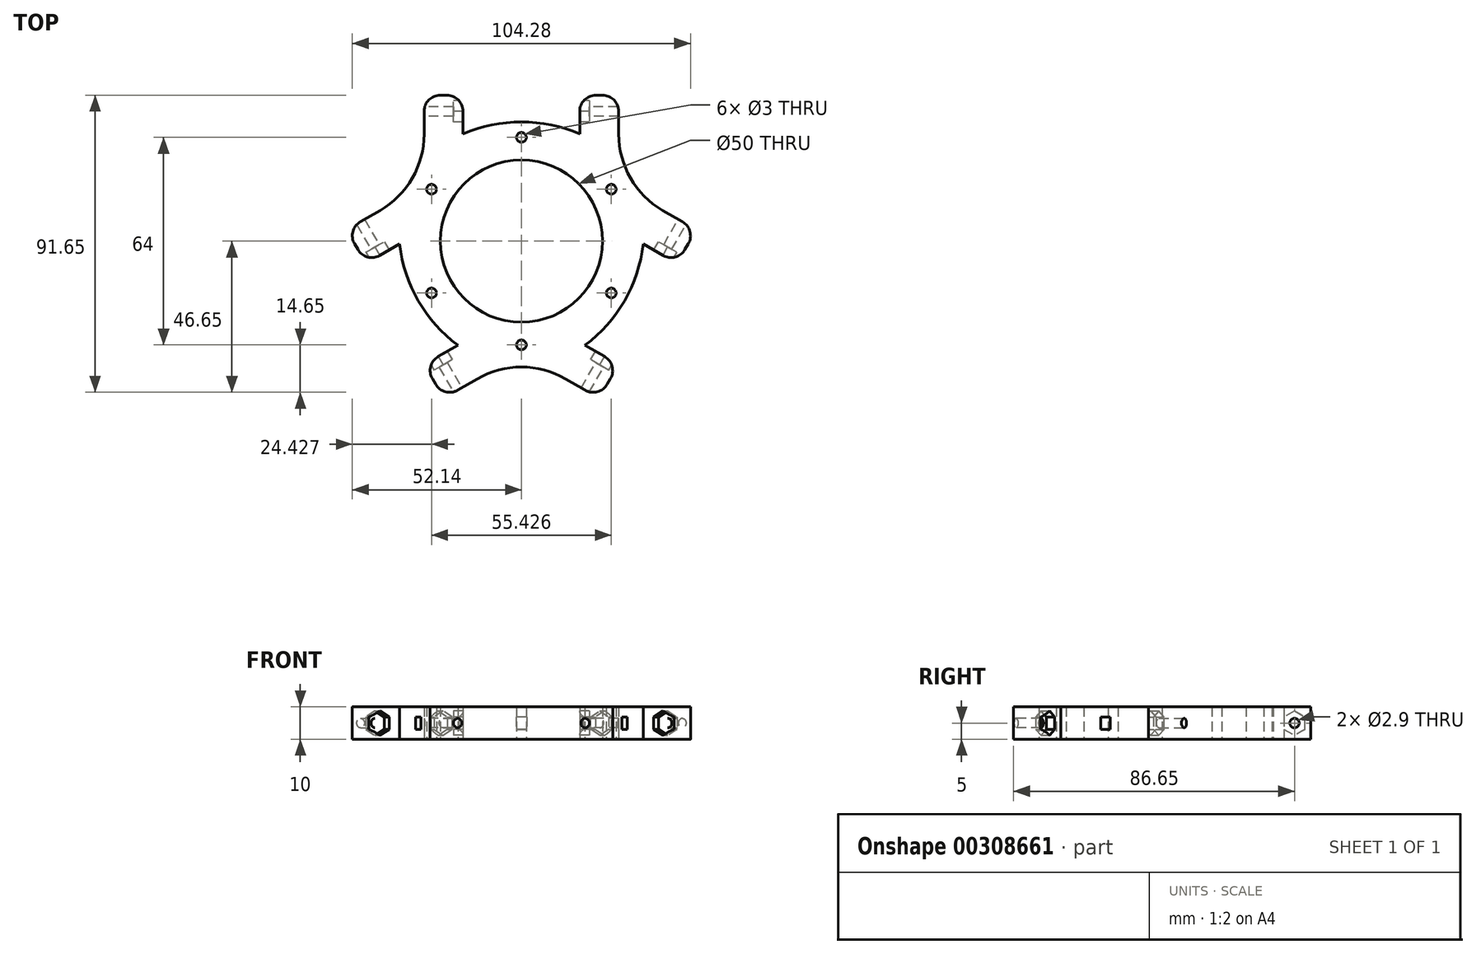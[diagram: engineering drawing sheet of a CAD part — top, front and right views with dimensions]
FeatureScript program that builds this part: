
annotation { "Feature Type Name" : "Feature", "Feature Type Description" : "" }
export const myFeature = defineFeature(function(context is Context, id is Id, definition is map)
    precondition{}
    {
        {
            var Q0;
            Q0=qCreatedBy(makeId("Top.planeOp"),FACE);
            var sketch = newSketch(context, id + "F0", { "sketchPlane" : qUnion([Q0])});
            skLineSegment(sketch, "E0", {"start": v(0, 0) * mm, "end": v(0, 45) * mm});
            skLineSegment(sketch, "E1", {"start": v(0, 0) * mm, "end": v(-38.97, -22.5) * mm});
            skLineSegment(sketch, "E2", {"start": v(0, 0) * mm, "end": v(31.83, -18.38) * mm});
            skLineSegment(sketch, "E3", {"start": v(18, 45) * mm, "end": v(30, 45) * mm});
            skLineSegment(sketch, "E4.MirrorCS", {"start": v(-18, 45) * mm, "end": v(-30, 45) * mm});
            skLineSegment(sketch, "E5", {"start": v(-47.97, -6.91) * mm, "end": v(-53.97, 3.48) * mm});
            skLineSegment(sketch, "E6.MirrorCS", {"start": v(-29.97, -38.09) * mm, "end": v(-23.97, -48.48) * mm});
            skLineSegment(sketch, "E7", {"start": v(47.97, -6.91) * mm, "end": v(53.97, 3.48) * mm});
            skLineSegment(sketch, "E8.MirrorCS", {"start": v(29.97, -38.09) * mm, "end": v(23.97, -48.48) * mm});
            skLineSegment(sketch, "E9", {"start": v(-30, 45) * mm, "end": v(-30, 33) * mm});
            skLineSegment(sketch, "E10", {"start": v(-53.97, 3.48) * mm, "end": v(-43.58, 9.48) * mm});
            skLineSegment(sketch, "E11", {"start": v(23.97, -48.48) * mm, "end": v(13.58, -42.48) * mm});
            skLineSegment(sketch, "E12.MirrorCS", {"start": v(30, 45) * mm, "end": v(30, 33) * mm});
            skLineSegment(sketch, "E13.MirrorCS", {"start": v(-23.97, -48.48) * mm, "end": v(-13.58, -42.48) * mm});
            skLineSegment(sketch, "E14.MirrorCS", {"start": v(53.97, 3.48) * mm, "end": v(43.58, 9.48) * mm});
            skCircle(sketch, "E15", {"center": v(0, 0) * mm, "radius": 25 * mm});
            skLineSegment(sketch, "E16", {"start": v(0, 0) * mm, "end": v(33.64, 19.42) * mm});
            skLineSegment(sketch, "E17", {"start": v(0, 0) * mm, "end": v(-33.64, 19.42) * mm});
            skLineSegment(sketch, "E18", {"start": v(0, 0) * mm, "end": v(0, -42.48) * mm});
            skCircle(sketch, "E19", {"center": v(27.71, 16) * mm, "radius": 1.5 * mm});
            skCircle(sketch, "E20", {"center": v(0, -32) * mm, "radius": 1.5 * mm});
            skCircle(sketch, "E21", {"center": v(-27.71, 16) * mm, "radius": 1.5 * mm});
            skLineSegment(sketch, "E22", {"start": v(18, 45) * mm, "end": v(18, 33) * mm});
            skLineSegment(sketch, "E23.MirrorCS", {"start": v(-18, 45) * mm, "end": v(-18, 33) * mm});
            skArc(sketch, "E24", {"start": v(18, 33) * mm, "mid": v(0, 36.76) * mm, "end": v(-18, 33) * mm});
            skLineSegment(sketch, "E25", {"start": v(47.97, -6.91) * mm, "end": v(37.58, -0.91) * mm});
            skLineSegment(sketch, "E26.MirrorCS", {"start": v(29.97, -38.09) * mm, "end": v(19.58, -32.09) * mm});
            skArc(sketch, "E27", {"start": v(19.58, -32.09) * mm, "mid": v(31.83, -18.38) * mm, "end": v(37.58, -0.91) * mm});
            skLineSegment(sketch, "E28", {"start": v(-29.97, -38.09) * mm, "end": v(-19.58, -32.09) * mm});
            skLineSegment(sketch, "E29.MirrorCS", {"start": v(-47.97, -6.91) * mm, "end": v(-37.58, -0.91) * mm});
            skArc(sketch, "E30", {"start": v(-37.58, -0.91) * mm, "mid": v(-31.83, -18.38) * mm, "end": v(-19.58, -32.09) * mm});
            skArc(sketch, "E31", {"start": v(-43.58, 9.48) * mm, "mid": v(-33.64, 19.42) * mm, "end": v(-30, 33) * mm});
            skArc(sketch, "E32", {"start": v(30, 33) * mm, "mid": v(33.64, 19.42) * mm, "end": v(43.58, 9.48) * mm});
            skArc(sketch, "E33", {"start": v(13.58, -42.48) * mm, "mid": v(0, -38.84) * mm, "end": v(-13.58, -42.48) * mm});
            skPoint(sketch, "E34.orphan", {"position": v(-36.79, 21.24) * mm});
            skPoint(sketch, "E35.orphan", {"position": v(0, 45) * mm});
            skPoint(sketch, "E36.orphan", {"position": v(-38.97, -22.5) * mm});
            skCircle(sketch, "E37", {"center": v(-27.71, -16) * mm, "radius": 1.5 * mm});
            skCircle(sketch, "E38", {"center": v(27.71, -16) * mm, "radius": 1.5 * mm});
            skCircle(sketch, "E39", {"center": v(0, 32) * mm, "radius": 1.5 * mm});
            skSolve(sketch);
        }
        {
            var Q0;
            {var subQ4=sQuery(id+"F0.wireOp",EDGE,"E4.MirrorCS");Q0=makeQuery(id+"F0.imprint","IMPRINT",FACE,{"disambiguationData":[TD([[makeQuery(id+"F0.imprint","IMPRINT",EDGE,{"derivedFrom":subQ4}),1.0]])]});}
            var Q1;
            {var subQ0=sQuery(id+"F0.wireOp",EDGE,"E6.MirrorCS");Q1=makeQuery(id+"F0.imprint","IMPRINT",FACE,{"disambiguationData":[TD([[makeQuery(id+"F0.imprint","IMPRINT",EDGE,{"derivedFrom":subQ0}),1.0]])]});}
            var Q2;
            {var subQ4=sQuery(id+"F0.wireOp",EDGE,"E3");Q2=makeQuery(id+"F0.imprint","IMPRINT",FACE,{"disambiguationData":[TD([[makeQuery(id+"F0.imprint","IMPRINT",EDGE,{"derivedFrom":subQ4}),-1.0]])]});}
            var Q3;
            {var subQ1=sQuery(id+"F0.wireOp",EDGE,"E7");Q3=makeQuery(id+"F0.imprint","IMPRINT",FACE,{"disambiguationData":[TD([[makeQuery(id+"F0.imprint","IMPRINT",EDGE,{"derivedFrom":subQ1}),1.0]])]});}
            var Q4;
            Q4=makeQuery(id+"F0.imprint","IMPRINT",FACE,{"disambiguationData":[TD([[makeQuery(id+"F0.imprint","IMPRINT",EDGE,{"derivedFrom":sQuery(id+"F0.wireOp",EDGE,"93i2Dirp-5Tey-j3A0-DUrq-3imIRp9fQiXa")}),1.0]])]});
            var Q5;
            {var subQ0=sQuery(id+"F0.wireOp",EDGE,"E1");var subQ1=sQuery(id+"F0.wireOp",EDGE,"7GjnHj9b-fa3a-kwGP-agom-r8laERjyn4mw");var subQ2=makeQuery(id+"F0.imprint","INTERSECT",VERTEX,{"derivedFrom":[subQ1,subQ0]});Q5=makeQuery(id+"F0.imprint","IMPRINT",FACE,{"disambiguationData":[TD([[makeQuery(id+"F0.imprint","IMPRINT",EDGE,{"disambiguationData":[TD([[subQ2,1.0]])],"derivedFrom":subQ1}),1.0]])]});}
            var Q6;
            {var subQ0=sQuery(id+"F0.wireOp",EDGE,"E0");var subQ1=sQuery(id+"F0.wireOp",EDGE,"7GjnHj9b-fa3a-kwGP-agom-r8laERjyn4mw");var subQ2=makeQuery(id+"F0.imprint","INTERSECT",VERTEX,{"derivedFrom":[subQ1,subQ0]});Q6=makeQuery(id+"F0.imprint","IMPRINT",FACE,{"disambiguationData":[TD([[makeQuery(id+"F0.imprint","IMPRINT",EDGE,{"disambiguationData":[TD([[subQ2,1.0]])],"derivedFrom":subQ1}),1.0]])]});}
            var Q7;
            {var subQ0=sQuery(id+"F0.wireOp",EDGE,"E1");var subQ1=sQuery(id+"F0.wireOp",EDGE,"7GjnHj9b-fa3a-kwGP-agom-r8laERjyn4mw");var subQ2=makeQuery(id+"F0.imprint","INTERSECT",VERTEX,{"derivedFrom":[subQ1,subQ0]});Q7=makeQuery(id+"F0.imprint","IMPRINT",FACE,{"disambiguationData":[TD([[makeQuery(id+"F0.imprint","IMPRINT",EDGE,{"disambiguationData":[TD([[subQ2,-1.0]])],"derivedFrom":subQ1}),1.0]])]});}
            var Q8;
            {var subQ4=sQuery(id+"F0.wireOp",EDGE,"E5");Q8=makeQuery(id+"F0.imprint","IMPRINT",FACE,{"disambiguationData":[TD([[makeQuery(id+"F0.imprint","IMPRINT",EDGE,{"derivedFrom":subQ4}),-1.0]])]});}
            var Q9;
            {var subQ4=sQuery(id+"F0.wireOp",EDGE,"E8.MirrorCS");Q9=makeQuery(id+"F0.imprint","IMPRINT",FACE,{"disambiguationData":[TD([[makeQuery(id+"F0.imprint","IMPRINT",EDGE,{"derivedFrom":subQ4}),-1.0]])]});}
            extrude(context, id + "F1", {"entities" : qUnion([Q0, Q1, Q2, Q3, Q4, Q5, Q6, Q7, Q8, Q9]), "depth" : 10 * mm});
        }
        {
            var Q0;
            Q0=qCreatedBy(makeId("Right.planeOp"),FACE);
            var sketch = newSketch(context, id + "F2", { "sketchPlane" : qUnion([Q0])});
            skCircle(sketch, "E40", {"center": v(40, 5) * mm, "radius": 1.45 * mm});
            skCircle(sketch, "E41.cCircle", {"center": v(40, 5) * mm, "radius": 3.28 * mm, "construction": true});
            skLineSegment(sketch, "E41.0", {"start": v(43.28, 6.9) * mm, "end": v(43.28, 3.1) * mm});
            skLineSegment(sketch, "E41.1", {"start": v(43.27, 3.1) * mm, "end": v(40, 1.22) * mm});
            skLineSegment(sketch, "E41.2", {"start": v(40, 1.22) * mm, "end": v(36.72, 3.1) * mm});
            skLineSegment(sketch, "E41.3", {"start": v(36.72, 3.1) * mm, "end": v(36.72, 6.9) * mm});
            skLineSegment(sketch, "E41.4", {"start": v(36.72, 6.9) * mm, "end": v(40, 8.78) * mm});
            skLineSegment(sketch, "E41.5", {"start": v(40, 8.78) * mm, "end": v(43.28, 6.9) * mm});
            skPoint(sketch, "E41.0.midPoint", {"position": v(43.28, 5) * mm});
            skSolve(sketch);
        }
        {
            var Q0;
            Q0=makeQuery(id+"F2.imprint","IMPRINT",FACE,{"disambiguationData":[TD([[makeQuery(id+"F2.imprint","IMPRINT",EDGE,{"derivedFrom":sQuery(id+"F2.wireOp",EDGE,"E40")}),1.0]])]});
            extrude(context, id + "F3", {"entities" : qUnion([Q0]), "depth" : 30 * mm, "hasSecondDirection" : true, "secondDirectionOppositeDirection" : true, "secondDirectionDepth" : 30 * mm});
        }
        {
            var Q0;
            Q0=makeQuery(id+"F3.opExtrude","SWEPT_BODY",BODY,{"disambiguationData":[OSD([sQuery(id+"F2.wireOp",EDGE,"E40")])]});
            var Q1;
            Q1=makeQuery(id+"F1.opExtrude","CAP_EDGE",EDGE,{"disambiguationData":[OSD([sQuery(id+"F0.wireOp",EDGE,"E15")])],"isStart":false});
            transform(context, id + "F4", {"entities" : qUnion([Q0]), "transformType" : TransformType.ROTATION, "transformAxis" : qUnion([Q1]), "angle" : 120 * degree, "makeCopy" : true});
        }
        {
            var Q0;
            Q0=makeQuery(id+"F4.opPattern","COPY",BODY,{"derivedFrom":makeQuery(id+"F3.opExtrude","SWEPT_BODY",BODY,{"disambiguationData":[OSD([sQuery(id+"F2.wireOp",EDGE,"E40")])]}),"instanceName":"1"});
            var Q1;
            Q1=makeQuery(id+"F1.opExtrude","CAP_EDGE",EDGE,{"disambiguationData":[OSD([sQuery(id+"F0.wireOp",EDGE,"E15")])],"isStart":false});
            transform(context, id + "F5", {"entities" : qUnion([Q0]), "transformType" : TransformType.ROTATION, "transformAxis" : qUnion([Q1]), "angle" : 120 * degree, "makeCopy" : true});
        }
        {
            var Q0;
            Q0=makeQuery(id+"F5.opPattern","COPY",BODY,{"derivedFrom":makeQuery(id+"F4.opPattern","COPY",BODY,{"derivedFrom":makeQuery(id+"F3.opExtrude","SWEPT_BODY",BODY,{"disambiguationData":[OSD([sQuery(id+"F2.wireOp",EDGE,"E40")])]}),"instanceName":"1"}),"instanceName":"1"});
            var Q1;
            Q1=makeQuery(id+"F3.opExtrude","SWEPT_BODY",BODY,{"disambiguationData":[OSD([sQuery(id+"F2.wireOp",EDGE,"E40")])]});
            var Q2;
            Q2=makeQuery(id+"F4.opPattern","COPY",BODY,{"derivedFrom":makeQuery(id+"F3.opExtrude","SWEPT_BODY",BODY,{"disambiguationData":[OSD([sQuery(id+"F2.wireOp",EDGE,"E40")])]}),"instanceName":"1"});
            var Q3;
            Q3=makeQuery(id+"F1.opExtrude","SWEPT_BODY",BODY,{"disambiguationData":[OSD([sQuery(id+"F0.wireOp",EDGE,"E3"),sQuery(id+"F0.wireOp",EDGE,"E4.MirrorCS"),sQuery(id+"F0.wireOp",EDGE,"E5"),sQuery(id+"F0.wireOp",EDGE,"E6.MirrorCS"),sQuery(id+"F0.wireOp",EDGE,"E7"),sQuery(id+"F0.wireOp",EDGE,"E8.MirrorCS"),sQuery(id+"F0.wireOp",EDGE,"E9"),sQuery(id+"F0.wireOp",EDGE,"E10"),sQuery(id+"F0.wireOp",EDGE,"E11"),sQuery(id+"F0.wireOp",EDGE,"E12.MirrorCS"),sQuery(id+"F0.wireOp",EDGE,"E13.MirrorCS"),sQuery(id+"F0.wireOp",EDGE,"E14.MirrorCS"),sQuery(id+"F0.wireOp",EDGE,"2t7xqRWb-bub8-eMNz-FE5e-p0023Oxu7Jbf"),sQuery(id+"F0.wireOp",EDGE,"vDAQe0BX-fdkM-CdWa-sWsN-lsCfwyhql2Up"),sQuery(id+"F0.wireOp",EDGE,"93i2Dirp-5Tey-j3A0-DUrq-3imIRp9fQiXa"),sQuery(id+"F0.wireOp",EDGE,"QqLDhM0M-4ZeX-t9WL-vnuS-0Zj9XB7gyNKe")])]});
            booleanBodies(context, id + "F6", {"operationType" : BooleanOperationType.SUBTRACTION, "tools" : qUnion([Q0, Q1, Q2]), "targets" : qUnion([Q3])});
        }
        {
            var Q0;
            Q0=makeQuery(id+"F1.opExtrude","SWEPT_EDGE",EDGE,{"disambiguationData":[OSD([sQuery(id+"F0.wireOp",EDGE,"E6.MirrorCS"),sQuery(id+"F0.wireOp",EDGE,"E13.MirrorCS")])]});
            var Q1;
            Q1=makeQuery(id+"F1.opExtrude","SWEPT_EDGE",EDGE,{"disambiguationData":[OSD([sQuery(id+"F0.wireOp",EDGE,"E8.MirrorCS"),sQuery(id+"F0.wireOp",EDGE,"E11")])]});
            var Q2;
            Q2=makeQuery(id+"F1.opExtrude","SWEPT_EDGE",EDGE,{"disambiguationData":[OSD([sQuery(id+"F0.wireOp",EDGE,"E7"),sQuery(id+"F0.wireOp",EDGE,"E14.MirrorCS")])]});
            var Q3;
            Q3=makeQuery(id+"F1.opExtrude","SWEPT_EDGE",EDGE,{"disambiguationData":[OSD([sQuery(id+"F0.wireOp",EDGE,"E3"),sQuery(id+"F0.wireOp",EDGE,"E12.MirrorCS")])]});
            var Q4;
            Q4=makeQuery(id+"F1.opExtrude","SWEPT_EDGE",EDGE,{"disambiguationData":[OSD([sQuery(id+"F0.wireOp",EDGE,"E4.MirrorCS"),sQuery(id+"F0.wireOp",EDGE,"E9")])]});
            var Q5;
            Q5=makeQuery(id+"F1.opExtrude","SWEPT_EDGE",EDGE,{"disambiguationData":[OSD([sQuery(id+"F0.wireOp",EDGE,"E5"),sQuery(id+"F0.wireOp",EDGE,"E10")])]});
            var Q6;
            Q6=makeQuery(id+"F1.opExtrude","SWEPT_EDGE",EDGE,{"disambiguationData":[OSD([sQuery(id+"F0.wireOp",EDGE,"E8.MirrorCS"),sQuery(id+"F0.wireOp",EDGE,"E26.MirrorCS")])]});
            var Q7;
            Q7=makeQuery(id+"F1.opExtrude","SWEPT_EDGE",EDGE,{"disambiguationData":[OSD([sQuery(id+"F0.wireOp",EDGE,"E7"),sQuery(id+"F0.wireOp",EDGE,"E25")])]});
            var Q8;
            Q8=makeQuery(id+"F1.opExtrude","SWEPT_EDGE",EDGE,{"disambiguationData":[OSD([sQuery(id+"F0.wireOp",EDGE,"E3"),sQuery(id+"F0.wireOp",EDGE,"E22")])]});
            var Q9;
            Q9=makeQuery(id+"F1.opExtrude","SWEPT_EDGE",EDGE,{"disambiguationData":[OSD([sQuery(id+"F0.wireOp",EDGE,"E4.MirrorCS"),sQuery(id+"F0.wireOp",EDGE,"E23.MirrorCS")])]});
            var Q10;
            Q10=makeQuery(id+"F1.opExtrude","SWEPT_EDGE",EDGE,{"disambiguationData":[OSD([sQuery(id+"F0.wireOp",EDGE,"E5"),sQuery(id+"F0.wireOp",EDGE,"E29.MirrorCS")])]});
            var Q11;
            Q11=makeQuery(id+"F1.opExtrude","SWEPT_EDGE",EDGE,{"disambiguationData":[OSD([sQuery(id+"F0.wireOp",EDGE,"E6.MirrorCS"),sQuery(id+"F0.wireOp",EDGE,"E28")])]});
            fillet(context, id + "F7", {"entities" : qUnion([Q0, Q1, Q2, Q3, Q4, Q5, Q6, Q7, Q8, Q9, Q10, Q11]), "radius" : 5 * mm, "tangentPropagation" : true, "allowEdgeOverflow" : false});
        }
        {
            var Q0;
            Q0=makeQuery(id+"F2.imprint","IMPRINT",FACE,{"disambiguationData":[TD([[makeQuery(id+"F2.imprint","IMPRINT",EDGE,{"derivedFrom":sQuery(id+"F2.wireOp",EDGE,"E40")}),-1.0]])]});
            extrude(context, id + "F8", {"entities" : qUnion([Q0]), "depth" : 21 * mm, "hasSecondDirection" : true, "secondDirectionOppositeDirection" : true, "secondDirectionDepth" : 21 * mm});
        }
        {
            var Q0;
            Q0=makeQuery(id+"F8.opExtrude","SWEPT_BODY",BODY,{"disambiguationData":[OSD([sQuery(id+"F2.wireOp",EDGE,"E40"),sQuery(id+"F2.wireOp",EDGE,"E41.0"),sQuery(id+"F2.wireOp",EDGE,"E41.1"),sQuery(id+"F2.wireOp",EDGE,"E41.2"),sQuery(id+"F2.wireOp",EDGE,"E41.3"),sQuery(id+"F2.wireOp",EDGE,"E41.4"),sQuery(id+"F2.wireOp",EDGE,"E41.5")])]});
            var Q1;
            Q1=makeQuery(id+"F1.opExtrude","CAP_EDGE",EDGE,{"disambiguationData":[OSD([sQuery(id+"F0.wireOp",EDGE,"E15")])],"isStart":false});
            transform(context, id + "F9", {"entities" : qUnion([Q0]), "transformType" : TransformType.ROTATION, "transformAxis" : qUnion([Q1]), "angle" : 120 * degree, "makeCopy" : true});
        }
        {
            var Q0;
            Q0=makeQuery(id+"F9.opPattern","COPY",BODY,{"derivedFrom":makeQuery(id+"F8.opExtrude","SWEPT_BODY",BODY,{"disambiguationData":[OSD([sQuery(id+"F2.wireOp",EDGE,"E40"),sQuery(id+"F2.wireOp",EDGE,"E41.0"),sQuery(id+"F2.wireOp",EDGE,"E41.1"),sQuery(id+"F2.wireOp",EDGE,"E41.2"),sQuery(id+"F2.wireOp",EDGE,"E41.3"),sQuery(id+"F2.wireOp",EDGE,"E41.4"),sQuery(id+"F2.wireOp",EDGE,"E41.5")])]}),"instanceName":"1"});
            var Q1;
            Q1=makeQuery(id+"F1.opExtrude","CAP_EDGE",EDGE,{"disambiguationData":[OSD([sQuery(id+"F0.wireOp",EDGE,"E15")])],"isStart":false});
            transform(context, id + "F10", {"entities" : qUnion([Q0]), "transformType" : TransformType.ROTATION, "transformAxis" : qUnion([Q1]), "angle" : 120 * degree, "makeCopy" : true});
        }
        {
            var Q0;
            Q0=makeQuery(id+"F8.opExtrude","SWEPT_BODY",BODY,{"disambiguationData":[OSD([sQuery(id+"F2.wireOp",EDGE,"E40"),sQuery(id+"F2.wireOp",EDGE,"E41.0"),sQuery(id+"F2.wireOp",EDGE,"E41.1"),sQuery(id+"F2.wireOp",EDGE,"E41.2"),sQuery(id+"F2.wireOp",EDGE,"E41.3"),sQuery(id+"F2.wireOp",EDGE,"E41.4"),sQuery(id+"F2.wireOp",EDGE,"E41.5")])]});
            var Q1;
            Q1=makeQuery(id+"F10.opPattern","COPY",BODY,{"derivedFrom":makeQuery(id+"F9.opPattern","COPY",BODY,{"derivedFrom":makeQuery(id+"F8.opExtrude","SWEPT_BODY",BODY,{"disambiguationData":[OSD([sQuery(id+"F2.wireOp",EDGE,"E40"),sQuery(id+"F2.wireOp",EDGE,"E41.0"),sQuery(id+"F2.wireOp",EDGE,"E41.1"),sQuery(id+"F2.wireOp",EDGE,"E41.2"),sQuery(id+"F2.wireOp",EDGE,"E41.3"),sQuery(id+"F2.wireOp",EDGE,"E41.4"),sQuery(id+"F2.wireOp",EDGE,"E41.5")])]}),"instanceName":"1"}),"instanceName":"1"});
            var Q2;
            Q2=makeQuery(id+"F9.opPattern","COPY",BODY,{"derivedFrom":makeQuery(id+"F8.opExtrude","SWEPT_BODY",BODY,{"disambiguationData":[OSD([sQuery(id+"F2.wireOp",EDGE,"E40"),sQuery(id+"F2.wireOp",EDGE,"E41.0"),sQuery(id+"F2.wireOp",EDGE,"E41.1"),sQuery(id+"F2.wireOp",EDGE,"E41.2"),sQuery(id+"F2.wireOp",EDGE,"E41.3"),sQuery(id+"F2.wireOp",EDGE,"E41.4"),sQuery(id+"F2.wireOp",EDGE,"E41.5")])]}),"instanceName":"1"});
            var Q3;
            Q3=makeQuery(id+"F1.opExtrude","SWEPT_BODY",BODY,{"disambiguationData":[OSD([sQuery(id+"F0.wireOp",EDGE,"E3"),sQuery(id+"F0.wireOp",EDGE,"E4.MirrorCS"),sQuery(id+"F0.wireOp",EDGE,"E5"),sQuery(id+"F0.wireOp",EDGE,"E6.MirrorCS"),sQuery(id+"F0.wireOp",EDGE,"E7"),sQuery(id+"F0.wireOp",EDGE,"E8.MirrorCS"),sQuery(id+"F0.wireOp",EDGE,"E9"),sQuery(id+"F0.wireOp",EDGE,"E10"),sQuery(id+"F0.wireOp",EDGE,"E11"),sQuery(id+"F0.wireOp",EDGE,"E12.MirrorCS"),sQuery(id+"F0.wireOp",EDGE,"E13.MirrorCS"),sQuery(id+"F0.wireOp",EDGE,"E14.MirrorCS"),sQuery(id+"F0.wireOp",EDGE,"E15"),sQuery(id+"F0.wireOp",EDGE,"E19"),sQuery(id+"F0.wireOp",EDGE,"E20"),sQuery(id+"F0.wireOp",EDGE,"E21"),sQuery(id+"F0.wireOp",EDGE,"E22"),sQuery(id+"F0.wireOp",EDGE,"E23.MirrorCS"),sQuery(id+"F0.wireOp",EDGE,"E24"),sQuery(id+"F0.wireOp",EDGE,"E25"),sQuery(id+"F0.wireOp",EDGE,"E26.MirrorCS"),sQuery(id+"F0.wireOp",EDGE,"E27"),sQuery(id+"F0.wireOp",EDGE,"E28"),sQuery(id+"F0.wireOp",EDGE,"E29.MirrorCS"),sQuery(id+"F0.wireOp",EDGE,"E30"),sQuery(id+"F0.wireOp",EDGE,"E31"),sQuery(id+"F0.wireOp",EDGE,"E32"),sQuery(id+"F0.wireOp",EDGE,"E33"),sQuery(id+"F0.wireOp",EDGE,"E37"),sQuery(id+"F0.wireOp",EDGE,"E38"),sQuery(id+"F0.wireOp",EDGE,"E39")])]});
            booleanBodies(context, id + "F11", {"operationType" : BooleanOperationType.SUBTRACTION, "tools" : qUnion([Q0, Q1, Q2]), "targets" : qUnion([Q3])});
        }
    });
